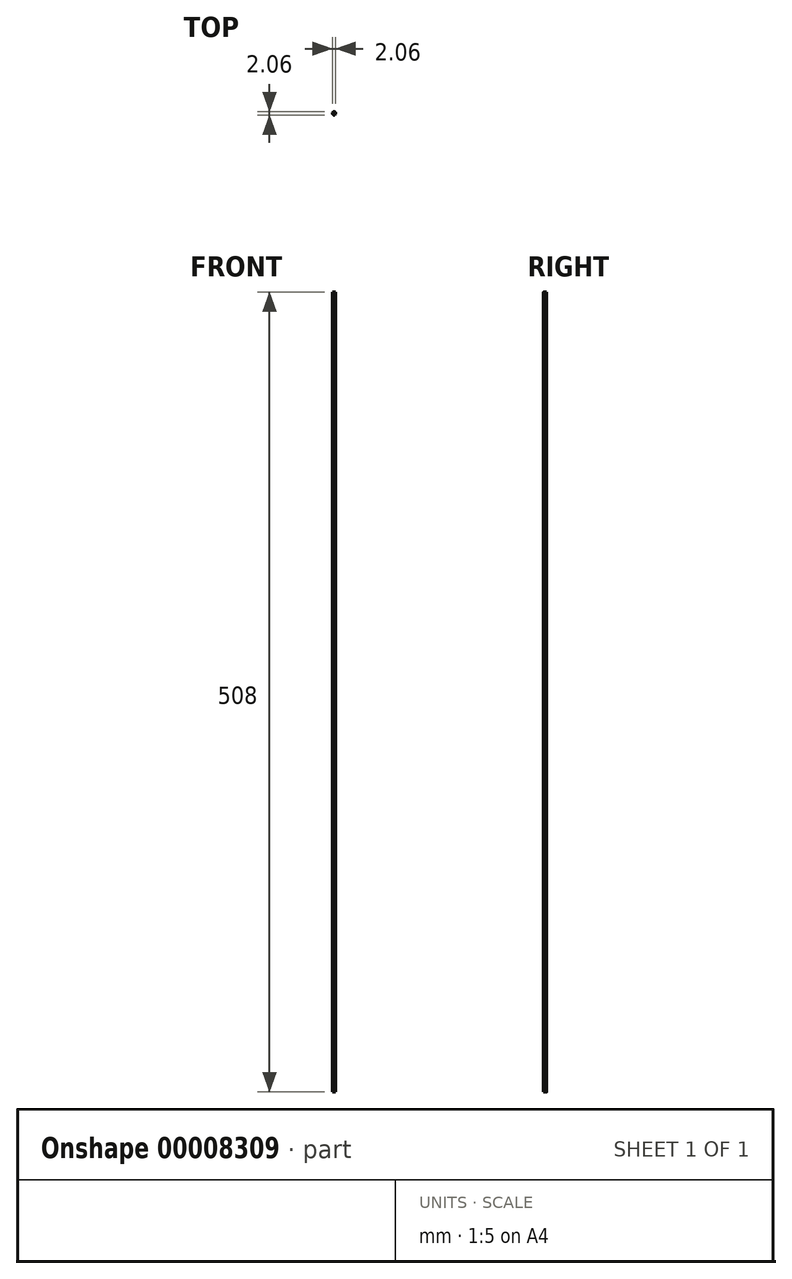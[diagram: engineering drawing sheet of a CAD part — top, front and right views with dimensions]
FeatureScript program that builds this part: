
annotation { "Feature Type Name" : "Feature", "Feature Type Description" : "" }
export const myFeature = defineFeature(function(context is Context, id is Id, definition is map)
    precondition{}
    {
        {
            var Q0;
            Q0=qCreatedBy(makeId("Top.planeOp"),FACE);
            var sketch = newSketch(context, id + "F0", { "sketchPlane" : qUnion([Q0])});
            skCircle(sketch, "E0", {"center": v(0, 0) * mm, "radius": 1.03 * mm});
            skSolve(sketch);
        }
        {
            var Q0;
            Q0 = qSketchRegion(id + "F0", true);
            extrude(context, id + "F1", {"entities" : qUnion([Q0]), "depth" : 508 * mm});
        }
    });
